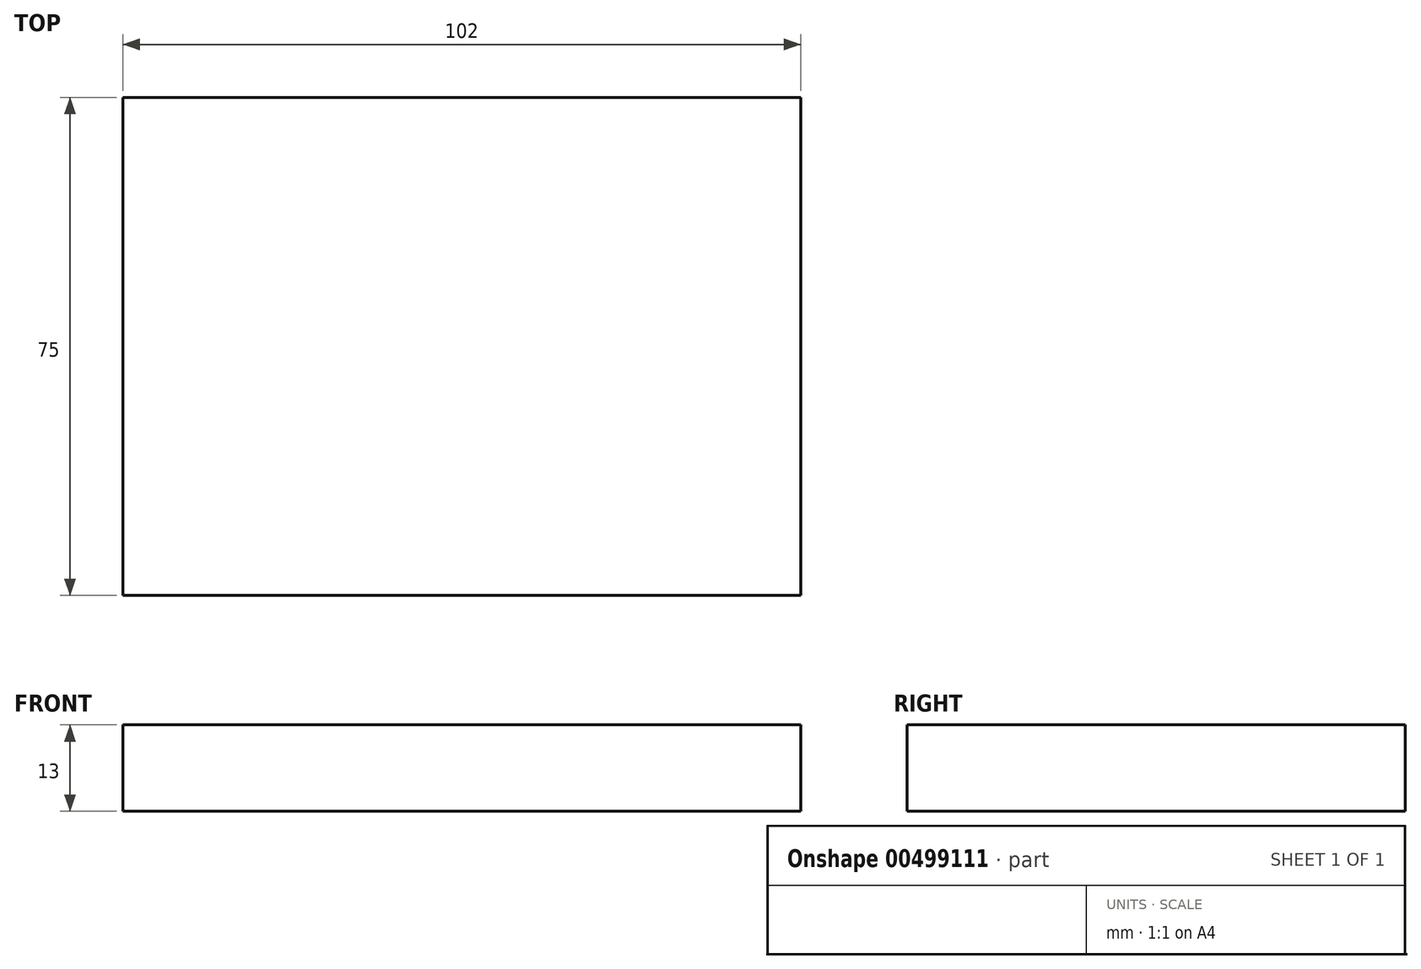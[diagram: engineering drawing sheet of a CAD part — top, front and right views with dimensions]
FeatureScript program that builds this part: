
annotation { "Feature Type Name" : "Feature", "Feature Type Description" : "" }
export const myFeature = defineFeature(function(context is Context, id is Id, definition is map)
    precondition{}
    {
        {
            var Q0;
            Q0=qCreatedBy(makeId("Top.planeOp"),FACE);
            var sketch = newSketch(context, id + "F0", { "sketchPlane" : qUnion([Q0])});
            skLineSegment(sketch, "E0.bottom", {"start": v(-51, 37.5) * mm, "end": v(51, 37.5) * mm});
            skLineSegment(sketch, "E0.top", {"start": v(-51, -37.5) * mm, "end": v(51, -37.5) * mm});
            skLineSegment(sketch, "E0.left", {"start": v(-51, 37.5) * mm, "end": v(-51, -37.5) * mm});
            skLineSegment(sketch, "E0.right", {"start": v(51, 37.5) * mm, "end": v(51, -37.5) * mm});
            skPoint(sketch, "E0.middle", {"position": v(0, 0) * mm});
            skSolve(sketch);
        }
        {
            var Q0;
            Q0 = qConstructionFilter(qBodyType(qCreatedBy(id + "F0" ,EDGE), BodyType.WIRE), ConstructionObject.NO);
            extrude(context, id + "F1", {"bodyType" : ToolBodyType.SURFACE, "surfaceEntities" : qUnion([Q0]), "depth" : 13 * mm});
        }
    });
